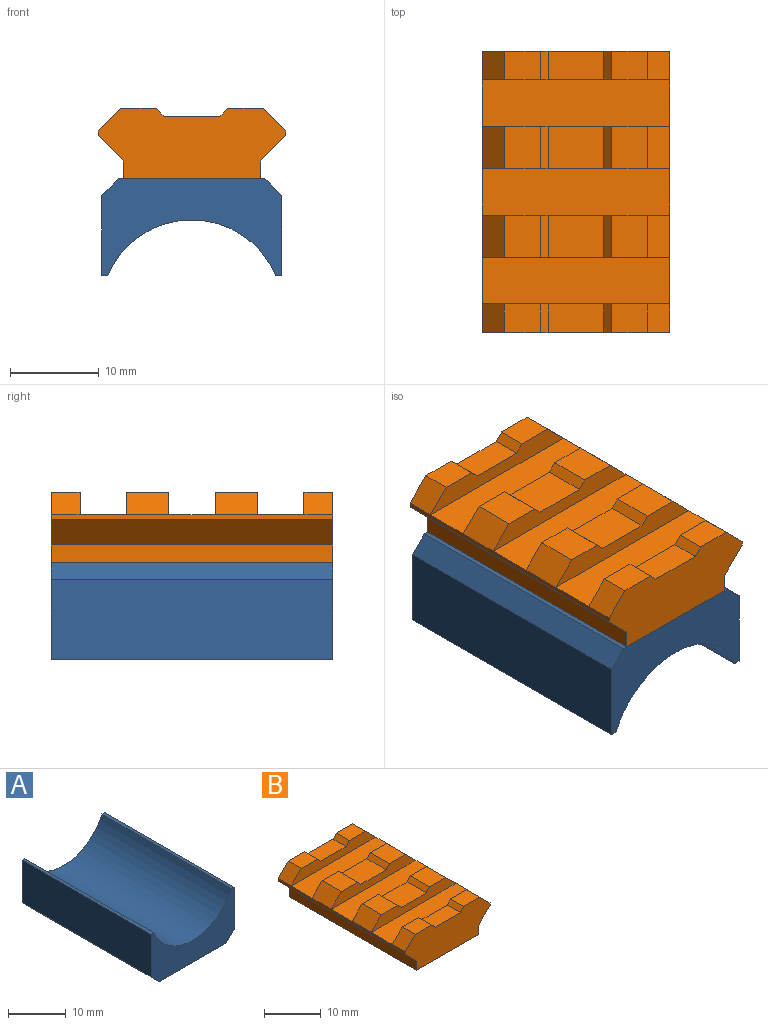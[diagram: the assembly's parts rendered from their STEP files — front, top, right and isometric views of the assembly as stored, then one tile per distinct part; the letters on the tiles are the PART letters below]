
ASSEMBLY  parts=2 mates=1
PART A: 10 faces, bbox 20.3x31.8x10.9 mm
  f0: plane 31.75x9.01mm, normal (-1,0,0), area 286.2mm2, adj f2,f4,f7,f8
  f1: plane 31.75x9.01mm, normal (1,0,0), area 286.2mm2, adj f2,f4,f6,f9
  f2: plane 20.32x10.92mm, normal (0,-1,0), area 132.5mm2, adj f0,f1,f3,f5,f6,f7,f8,f9
  f3: plane 31.75x16.51mm, normal (0,0,-1), area 524.2mm2, adj f2,f4,f6,f7
  f4: plane 20.32x10.92mm, normal (0,1,0), area 132.5mm2, adj f0,f1,f3,f5,f6,f7,f8,f9
  f5: cylinder r=10.3mm len=31.75mm, axis (0,-1,0), area 764.3mm2, adj f2,f4,f8,f9
  f6: plane 31.75x1.91mm, normal (0.71,0,-0.71), area 85.5mm2, adj f1,f2,f3,f4
  f7: plane 31.75x1.91mm, normal (-0.71,0,-0.71), area 85.5mm2, adj f0,f2,f3,f4
  f8: plane 31.75x0.68mm, normal (0,0,1), area 21.7mm2, adj f0,f2,f4,f5
  f9: plane 31.75x0.68mm, normal (0,0,1), area 21.7mm2, adj f1,f2,f4,f5
PART B: 46 faces, bbox 21.2x31.8x7.9 mm
  f0: plane 4.78x2.53mm, normal (0.71,0,0.71), area 17.1mm2, adj f3,f27,f42,f45
  f1: plane 4.78x2.53mm, normal (0.71,0,0.71), area 17.1mm2, adj f4,f27,f39,f41
  f2: plane 3.25x2.53mm, normal (0.71,0,0.71), area 11.6mm2, adj f5,f27,f35,f38
  f3: plane 4.78x4.06mm, normal (0,0,1), area 19.4mm2, adj f0,f6,f42,f45
  f4: plane 4.78x4.06mm, normal (0,0,1), area 19.4mm2, adj f1,f7,f39,f41
  f5: plane 4.06x3.25mm, normal (0,0,1), area 13.2mm2, adj f2,f8,f35,f38
  f6: plane 4.78x0.88mm, normal (-0.71,0,0.71), area 5.9mm2, adj f3,f9,f42,f45
  f7: plane 4.78x0.88mm, normal (-0.71,0,0.71), area 5.9mm2, adj f4,f10,f39,f41
  f8: plane 3.25x0.88mm, normal (-0.71,0,0.71), area 4mm2, adj f5,f11,f35,f38
  f9: plane 6.27x4.78mm, normal (0,0,1), area 30mm2, adj f6,f12,f42,f45
  f10: plane 6.27x4.78mm, normal (0,0,1), area 30mm2, adj f7,f13,f39,f41
  f11: plane 6.27x3.25mm, normal (0,0,1), area 20.4mm2, adj f8,f14,f35,f38
  f12: plane 4.78x0.88mm, normal (0.71,0,0.71), area 5.9mm2, adj f9,f15,f42,f45
  f13: plane 4.78x0.88mm, normal (0.71,0,0.71), area 5.9mm2, adj f10,f16,f39,f41
  f14: plane 3.25x0.88mm, normal (0.71,0,0.71), area 4mm2, adj f11,f17,f35,f38
  f15: plane 4.78x4.06mm, normal (0,0,1), area 19.4mm2, adj f12,f18,f42,f45
  f16: plane 4.78x4.06mm, normal (0,0,1), area 19.4mm2, adj f13,f19,f39,f41
  f17: plane 4.06x3.25mm, normal (0,0,1), area 13.2mm2, adj f14,f20,f35,f38
  f18: plane 4.78x2.53mm, normal (-0.71,0,0.71), area 17.1mm2, adj f15,f21,f42,f45
  f19: plane 4.78x2.53mm, normal (-0.71,0,0.71), area 17.1mm2, adj f16,f21,f39,f41
  f20: plane 3.25x2.53mm, normal (-0.71,0,0.71), area 11.6mm2, adj f17,f21,f35,f38
  f21: plane 31.75x0.54mm, normal (-1,0,0), area 17.1mm2, adj f18,f19,f20,f22,f34,f35,f36,f37
  f22: plane 31.75x2.85mm, normal (-0.71,0,-0.71), area 128mm2, adj f21,f23,f35,f36
  f23: plane 31.75x2mm, normal (-1,0,0), area 63.6mm2, adj f22,f24,f35,f36
  f24: plane 31.75x15.5mm, normal (0,0,-1), area 492.1mm2, adj f23,f25,f35,f36
  f25: plane 31.75x2mm, normal (1,0,0), area 63.6mm2, adj f24,f26,f35,f36
  f26: plane 31.75x2.85mm, normal (0.71,0,-0.71), area 128mm2, adj f25,f27,f35,f36
  f27: plane 31.75x0.54mm, normal (1,0,0), area 17.1mm2, adj f0,f1,f2,f26,f28,f35,f36,f37
  f28: plane 3.25x2.53mm, normal (0.71,0,0.71), area 11.6mm2, adj f27,f29,f36,f44
  f29: plane 4.06x3.25mm, normal (0,0,1), area 13.2mm2, adj f28,f30,f36,f44
  f30: plane 3.25x0.88mm, normal (-0.71,0,0.71), area 4mm2, adj f29,f31,f36,f44
  f31: plane 6.27x3.25mm, normal (0,0,1), area 20.4mm2, adj f30,f32,f36,f44
  f32: plane 3.25x0.88mm, normal (0.71,0,0.71), area 4mm2, adj f31,f33,f36,f44
  f33: plane 4.06x3.25mm, normal (0,0,1), area 13.2mm2, adj f32,f34,f36,f44
  f34: plane 3.25x2.53mm, normal (-0.71,0,0.71), area 11.6mm2, adj f21,f33,f36,f44
  f35: plane 21.2x7.92mm, normal (0,1,0), area 135.7mm2, adj f2,f5,f8,f11,f14,f17,f20,f21
  f36: plane 21.2x7.92mm, normal (0,-1,0), area 135.7mm2, adj f21,f22,f23,f24,f25,f26,f27,f28
  f37: plane 21.2x5.23mm, normal (0,0,1), area 110.9mm2, adj f21,f27,f38,f39
  f38: plane 21.2x2.53mm, normal (0,-1,0), area 41mm2, adj f2,f5,f8,f11,f14,f17,f20,f37
  f39: plane 21.2x2.53mm, normal (0,1,0), area 41mm2, adj f1,f4,f7,f10,f13,f16,f19,f37
  f40: plane 21.2x5.23mm, normal (0,0,1), area 110.9mm2, adj f21,f27,f41,f42
  f41: plane 21.2x2.53mm, normal (0,-1,0), area 41mm2, adj f1,f4,f7,f10,f13,f16,f19,f40
  f42: plane 21.2x2.53mm, normal (0,1,0), area 41mm2, adj f0,f3,f6,f9,f12,f15,f18,f40
  f43: plane 21.2x5.23mm, normal (0,0,1), area 110.9mm2, adj f21,f27,f44,f45
  f44: plane 21.2x2.53mm, normal (0,1,0), area 41mm2, adj f28,f29,f30,f31,f32,f33,f34,f43
  f45: plane 21.2x2.53mm, normal (0,-1,0), area 41mm2, adj f0,f3,f6,f9,f12,f15,f18,f43
PLACE A rot(axis=(0,1,0),180deg) t=(16.8,59.61,-10.48)mm
PLACE B t=(16.9,-7.09,12.34)mm
MATE planar B.f24 <-> A.f3  axis (0,0,-1) through (16.8,8.78,4.43)mm
